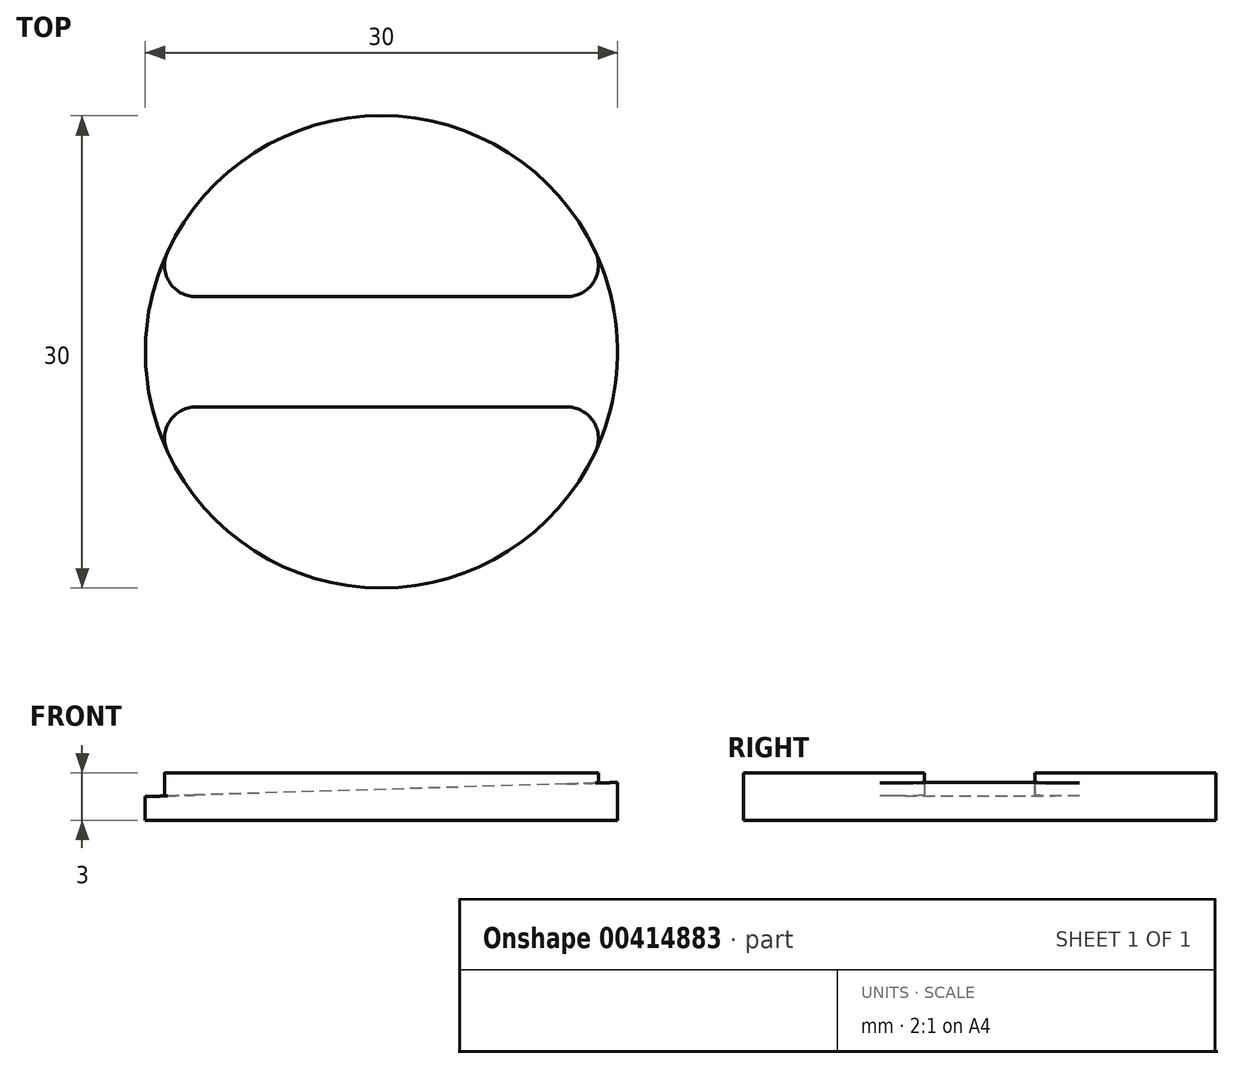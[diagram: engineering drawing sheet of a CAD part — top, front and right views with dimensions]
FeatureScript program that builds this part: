
annotation { "Feature Type Name" : "Feature", "Feature Type Description" : "" }
export const myFeature = defineFeature(function(context is Context, id is Id, definition is map)
    precondition{}
    {
        {
            var Q0;
            Q0=qCreatedBy(makeId("Top.planeOp"),FACE);
            var sketch = newSketch(context, id + "F0", { "sketchPlane" : qUnion([Q0])});
            skCircle(sketch, "E0", {"center": v(0, 0) * mm, "radius": 15 * mm});
            skSolve(sketch);
        }
        {
            var Q0;
            Q0=makeQuery(id+"F0.imprint","IMPRINT",FACE,{"disambiguationData":[TD([[makeQuery(id+"F0.imprint","IMPRINT",EDGE,{"derivedFrom":sQuery(id+"F0.wireOp",EDGE,"E0")}),1.0]])]});
            extrude(context, id + "F1", {"entities" : qUnion([Q0]), "depth" : 3 * mm});
        }
        {
            var Q0;
            Q0=qCreatedBy(makeId("Front.planeOp"),FACE);
            var sketch = newSketch(context, id + "F2", { "sketchPlane" : qUnion([Q0])});
            skLineSegment(sketch, "E1.0", {"start": v(-15, 3) * mm, "end": v(15, 3) * mm});
            skLineSegment(sketch, "E2", {"start": v(15, 3) * mm, "end": v(15, 2.4) * mm});
            skLineSegment(sketch, "E3", {"start": v(15, 2.4) * mm, "end": v(-15, 1.5) * mm});
            skLineSegment(sketch, "E4", {"start": v(-15, 1.5) * mm, "end": v(-15, 3) * mm});
            skLineSegment(sketch, "E5.0", {"start": v(-15, 0) * mm, "end": v(15, 0) * mm});
            skSolve(sketch);
        }
        {
            var Q0;
            {var subQ0=sQuery(id+"F2.wireOp",EDGE,"E2");Q0=makeQuery(id+"F2.imprint","IMPRINT",FACE,{"disambiguationData":[TD([[makeQuery(id+"F2.imprint","IMPRINT",EDGE,{"derivedFrom":subQ0}),-1.0]])]});}
            extrude(context, id + "F3", {"entities" : qUnion([Q0]), "operationType" : NewBodyOperationType.REMOVE, "endBound" : BoundingType.SYMMETRIC, "oppositeDirection" : true, "depth" : 7 * mm});
        }
        {
            var Q0;
            Q0=makeQuery(id+"F3.boolean.opBoolean","INTERSECT",EDGE,{"disambiguationData":[OD(0.0)],"derivedFrom":[makeQuery(id+"F1.opExtrude","SWEPT_FACE",FACE,{"disambiguationData":[OSD([sQuery(id+"F0.wireOp",EDGE,"E0")])]}),makeQuery(id+"F3.opExtrude","CAP_FACE",FACE,{"disambiguationData":[OSD([sQuery(id+"F2.wireOp",EDGE,"E1.0"),sQuery(id+"F2.wireOp",EDGE,"E2"),sQuery(id+"F2.wireOp",EDGE,"E3"),sQuery(id+"F2.wireOp",EDGE,"E4")])],"isStart":true})]});
            var Q1;
            Q1=makeQuery(id+"F3.boolean.opBoolean","INTERSECT",EDGE,{"disambiguationData":[OD(0.0)],"derivedFrom":[makeQuery(id+"F1.opExtrude","SWEPT_FACE",FACE,{"disambiguationData":[OSD([sQuery(id+"F0.wireOp",EDGE,"E0")])]}),makeQuery(id+"F3.opExtrude","CAP_FACE",FACE,{"disambiguationData":[OSD([sQuery(id+"F2.wireOp",EDGE,"E1.0"),sQuery(id+"F2.wireOp",EDGE,"E2"),sQuery(id+"F2.wireOp",EDGE,"E3"),sQuery(id+"F2.wireOp",EDGE,"E4")])],"isStart":false})]});
            var Q2;
            Q2=makeQuery(id+"F3.boolean.opBoolean","INTERSECT",EDGE,{"disambiguationData":[OD(1.0)],"derivedFrom":[makeQuery(id+"F1.opExtrude","SWEPT_FACE",FACE,{"disambiguationData":[OSD([sQuery(id+"F0.wireOp",EDGE,"E0")])]}),makeQuery(id+"F3.opExtrude","CAP_FACE",FACE,{"disambiguationData":[OSD([sQuery(id+"F2.wireOp",EDGE,"E1.0"),sQuery(id+"F2.wireOp",EDGE,"E2"),sQuery(id+"F2.wireOp",EDGE,"E3"),sQuery(id+"F2.wireOp",EDGE,"E4")])],"isStart":false})]});
            var Q3;
            Q3=makeQuery(id+"F3.boolean.opBoolean","INTERSECT",EDGE,{"disambiguationData":[OD(1.0)],"derivedFrom":[makeQuery(id+"F1.opExtrude","SWEPT_FACE",FACE,{"disambiguationData":[OSD([sQuery(id+"F0.wireOp",EDGE,"E0")])]}),makeQuery(id+"F3.opExtrude","CAP_FACE",FACE,{"disambiguationData":[OSD([sQuery(id+"F2.wireOp",EDGE,"E1.0"),sQuery(id+"F2.wireOp",EDGE,"E2"),sQuery(id+"F2.wireOp",EDGE,"E3"),sQuery(id+"F2.wireOp",EDGE,"E4")])],"isStart":true})]});
            fillet(context, id + "F4", {"entities" : qUnion([Q0, Q1, Q2, Q3]), "radius" : 2 * mm, "tangentPropagation" : true, "allowEdgeOverflow" : false});
        }
    });
